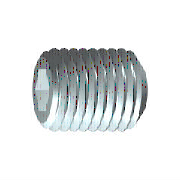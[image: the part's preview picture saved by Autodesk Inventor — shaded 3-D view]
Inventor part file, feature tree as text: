
AUTODESK INVENTOR PART (.ipt)
format: ipt  version: 2016 (Build 200138000, 138)  size: 167,424 bytes
history: native  units: mm (DEFAULTED — no unit token found)
features: sketch x2, extrude x1, other x1, plane x1
ambient origin geometry x8: Origin, YZ Plane, XZ Plane, XY Plane, X Axis, Y Axis, Z Axis, Center Point
bodies: Solid1 (feature_tree), Body (feature_tree)
feature tree (5):
  extrude  "Slot"  TaperAngle=60.0deg  [1 undecoded]
  other  "Work Axis1"
  plane  "Work Plane1"
  sketch  "Sketch1"  dims[d0=2.5mm d1=60.0deg]
  sketch  "Sketch2"  dims[d2=4.0mm d3=2.309401mm d6=90.0deg d4=0.0mm d5=5.0mm d7=0.429415mm d8=45.0deg d21=10.0mm d9=0.0mm d11=5.0mm d12=0.0mm d13=0.429415mm d14=45.0deg d15=0.0mm d29=0.429415mm d30=0.429415mm d31=0.0mm]
note: 1 required parameter value undecoded (feature->parameter linkage not recoverable at this tier; creation-order binding heuristic only, values carry confidence <= 0.55)
